# Revit family: HERZ Strömax Балансировочный клапан с измерительными клапанами, шпиндель прямой 4218 GF
name_source: partatom
category: Rohrzubehör
units: mm (PartAtom-declared; Revit-internal decimal feet)

## family parameters
Arbeitsebenenbasiert = Nein
Beim Laden mit Abzugskörper schneiden = Nein
Bemaßung runder Anschluss = Durchmesser verwenden
Gemeinsam genutzt = Nein
Immer vertikal = Ja
OmniClass-Nummer = 23.65.55.14
OmniClass-Titel = Valves for Liquid Services
Teiletyp = Unterbricht

## types (1)
- HERZ Strömax Балансировочный клапан с измерительными клапанами, шпиндель прямой 4218 GF
    GT = 10 mm  [stored 0.0328084 ft]
    Hersteller = HERZ Armaturen Ges.m.b.H.
    O-Ring = EPDM
    SCRNCODE = 05;07;02
    SCRNSEQ = ARM;ARM_TYP="STRV";2
    URL = www.herz-armaturen.ru
    Vorgabe-Ansicht = 0 mm  [stored 0 ft]
    W01 = 85.00°
    W02 = 60.00°
    Букса = чугун GJL 250 по EN 1561
    Измерение перепада давления = Балансировочный клапан Strömax GF оборудован двумя измерительными клапанами:
при использовании соответствующего измерительного прибора можно измерить перепад давления и благодаря этому можно соответственно определить расход в зависимости от степени настройки.
Кроме того, с HERZ измерительного компьютера можно непосредственно считывать показания расхода (см. инструкцию).
При использовании этиленгликоля, как средства от замерзания, меняется плотность теплоносителя, которую обязательно необходимо учитывать при измерениях перепада давления.
    Исполнение = Балансировочный клапан STRÖMAX-GF с измерительными клапанами DN 50 - 300:
Прямой шпиндель, корпус из серого чугуна GJL 250 по EN 1561, фланец согласно EN 1092, PN 16, окрашен в синий цвет.
Букса из серого чугуна GJL 250, с неподнимающимся шпинделем, уплотнение шпинделя с помощью тройного кольцевого уплотнения Цифровой указатель ступеней предварительной настройки.
    Кегель клапана = чугун GJL 250 по EN 1561/ EPDM с покрытием
    Корпус = чугун GJL 250 по EN 1561
    Макс. рабочая температура = 110 °C
    Макс. рабочее давление = 1600000.0 Pa
    Мин. рабочая температура = -10 °C
    Область применения = Для гидравлической балансировки в системах отопления или охлаждения, регулирования и перекрытия трубопроводов, стояков, теплообменников, тепловых и холодильных регистров.
    Регулировочный шпиндель = латунь / нержавеющая сталь
    Среда = Допускается использование этилен- и пропиленгликоля в концентрации смеси 25-50% объема.
Качество теплоносителя согласно ÖNORM H 5195 и VDI 2035.
    Счетное устройство = пластмасса
    Шпиндель (DN125 - DN300) = нержавеющая сталь
    Шпиндель (DN50 - DN100) = латунь

note: [stored X ft] marks values corroborated as IEEE doubles in the binary element streams (Revit-internal decimal feet)
